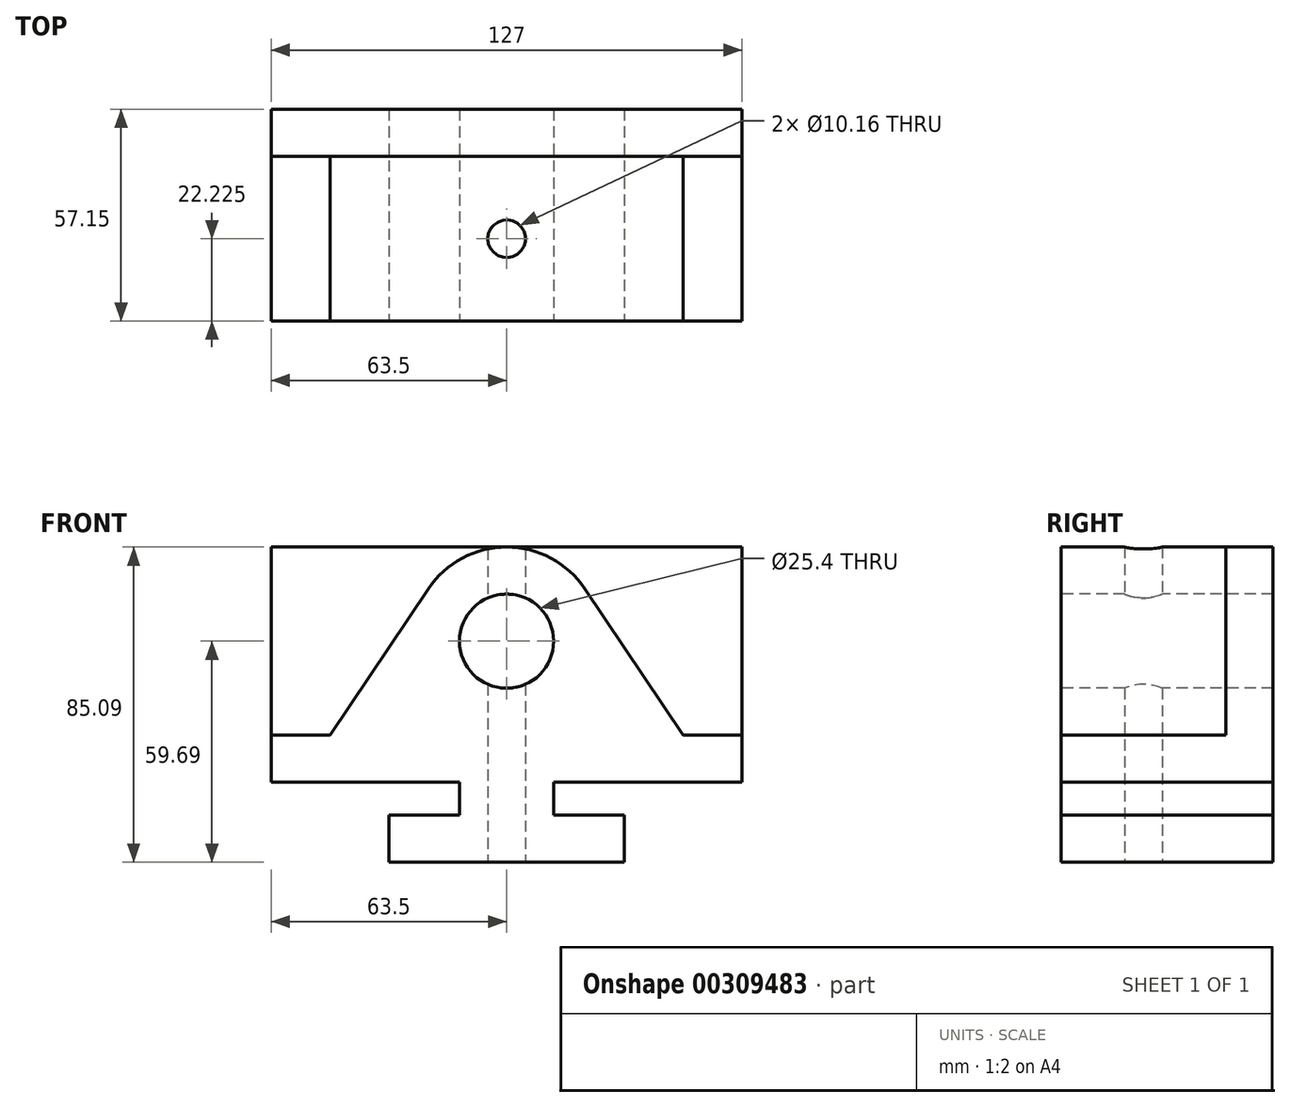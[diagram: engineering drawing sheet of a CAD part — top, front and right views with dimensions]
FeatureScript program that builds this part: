
annotation { "Feature Type Name" : "Feature", "Feature Type Description" : "" }
export const myFeature = defineFeature(function(context is Context, id is Id, definition is map)
    precondition{}
    {
        {
            var Q0;
            Q0=qCreatedBy(makeId("Front.planeOp"),FACE);
            var sketch = newSketch(context, id + "F0", { "sketchPlane" : qUnion([Q0])});
            skLineSegment(sketch, "E0", {"start": v(0, 0) * mm, "end": v(63.5, 0) * mm});
            skLineSegment(sketch, "E1", {"start": v(63.5, 0) * mm, "end": v(63.5, 12.7) * mm});
            skLineSegment(sketch, "E2", {"start": v(0, 0) * mm, "end": v(0, 12.7) * mm});
            skLineSegment(sketch, "E3", {"start": v(0, 12.7) * mm, "end": v(19.05, 12.7) * mm});
            skLineSegment(sketch, "E4", {"start": v(19.05, 12.7) * mm, "end": v(19.05, 21.59) * mm});
            skLineSegment(sketch, "E5", {"start": v(19.05, 21.59) * mm, "end": v(-31.75, 21.59) * mm});
            skLineSegment(sketch, "E6", {"start": v(-31.75, 21.59) * mm, "end": v(-31.75, 85.1) * mm});
            skLineSegment(sketch, "E7", {"start": v(-31.75, 85.09) * mm, "end": v(95.25, 85.1) * mm});
            skLineSegment(sketch, "E8", {"start": v(63.5, 12.7) * mm, "end": v(44.45, 12.7) * mm});
            skLineSegment(sketch, "E9", {"start": v(44.45, 12.7) * mm, "end": v(44.45, 21.59) * mm});
            skLineSegment(sketch, "E10", {"start": v(44.45, 21.59) * mm, "end": v(95.25, 21.6) * mm});
            skLineSegment(sketch, "E11", {"start": v(95.25, 21.6) * mm, "end": v(95.25, 85.1) * mm});
            skLineSegment(sketch, "E12", {"start": v(-31.75, 34.3) * mm, "end": v(-15.87, 34.3) * mm});
            skLineSegment(sketch, "E13", {"start": v(95.25, 34.3) * mm, "end": v(79.38, 34.3) * mm});
            skLineSegment(sketch, "E14", {"start": v(-15.88, 34.3) * mm, "end": v(10.66, 73.84) * mm});
            skLineSegment(sketch, "E15", {"start": v(79.38, 34.3) * mm, "end": v(52.84, 73.84) * mm});
            skArc(sketch, "E16", {"start": v(52.84, 73.84) * mm, "mid": v(31.75, 85.1) * mm, "end": v(10.66, 73.84) * mm});
            skCircle(sketch, "E17", {"center": v(31.75, 59.7) * mm, "radius": 12.7 * mm});
            skSolve(sketch);
        }
        {
            var Q0;
            {var subQ0=sQuery(id+"F0.wireOp",EDGE,"E12");Q0=makeQuery(id+"F0.imprint","IMPRINT",FACE,{"disambiguationData":[TD([[makeQuery(id+"F0.imprint","IMPRINT",EDGE,{"derivedFrom":subQ0}),1.0]])]});}
            var Q1;
            {var subQ1=sQuery(id+"F0.wireOp",EDGE,"E13");Q1=makeQuery(id+"F0.imprint","IMPRINT",FACE,{"disambiguationData":[TD([[makeQuery(id+"F0.imprint","IMPRINT",EDGE,{"derivedFrom":subQ1}),-1.0]])]});}
            var Q2;
            Q2=makeQuery(id+"F0.imprint","IMPRINT",FACE,{"disambiguationData":[TD([[makeQuery(id+"F0.imprint","IMPRINT",EDGE,{"derivedFrom":sQuery(id+"F0.wireOp",EDGE,"E0")}),1.0]])]});
            extrude(context, id + "F1", {"entities" : qUnion([Q0, Q1, Q2]), "oppositeDirection" : true, "depth" : 12.7 * mm});
        }
        {
            var Q0;
            Q0=makeQuery(id+"F0.imprint","IMPRINT",FACE,{"disambiguationData":[TD([[makeQuery(id+"F0.imprint","IMPRINT",EDGE,{"derivedFrom":sQuery(id+"F0.wireOp",EDGE,"E0")}),1.0]])]});
            extrude(context, id + "F2", {"entities" : qUnion([Q0]), "operationType" : NewBodyOperationType.ADD, "depth" : 44.45 * mm});
        }
        {
            var Q0;
            Q0=qCreatedBy(makeId("Top.planeOp"),FACE);
            var sketch = newSketch(context, id + "F3", { "sketchPlane" : qUnion([Q0])});
            skCircle(sketch, "E18", {"center": v(31.75, -22.23) * mm, "radius": 5.08 * mm});
            skSolve(sketch);
        }
        {
            var Q0;
            Q0 = qSketchRegion(id + "F3", true);
            extrude(context, id + "F4", {"entities" : qUnion([Q0]), "operationType" : NewBodyOperationType.REMOVE, "depth" : 199.39 * mm});
        }
    });
